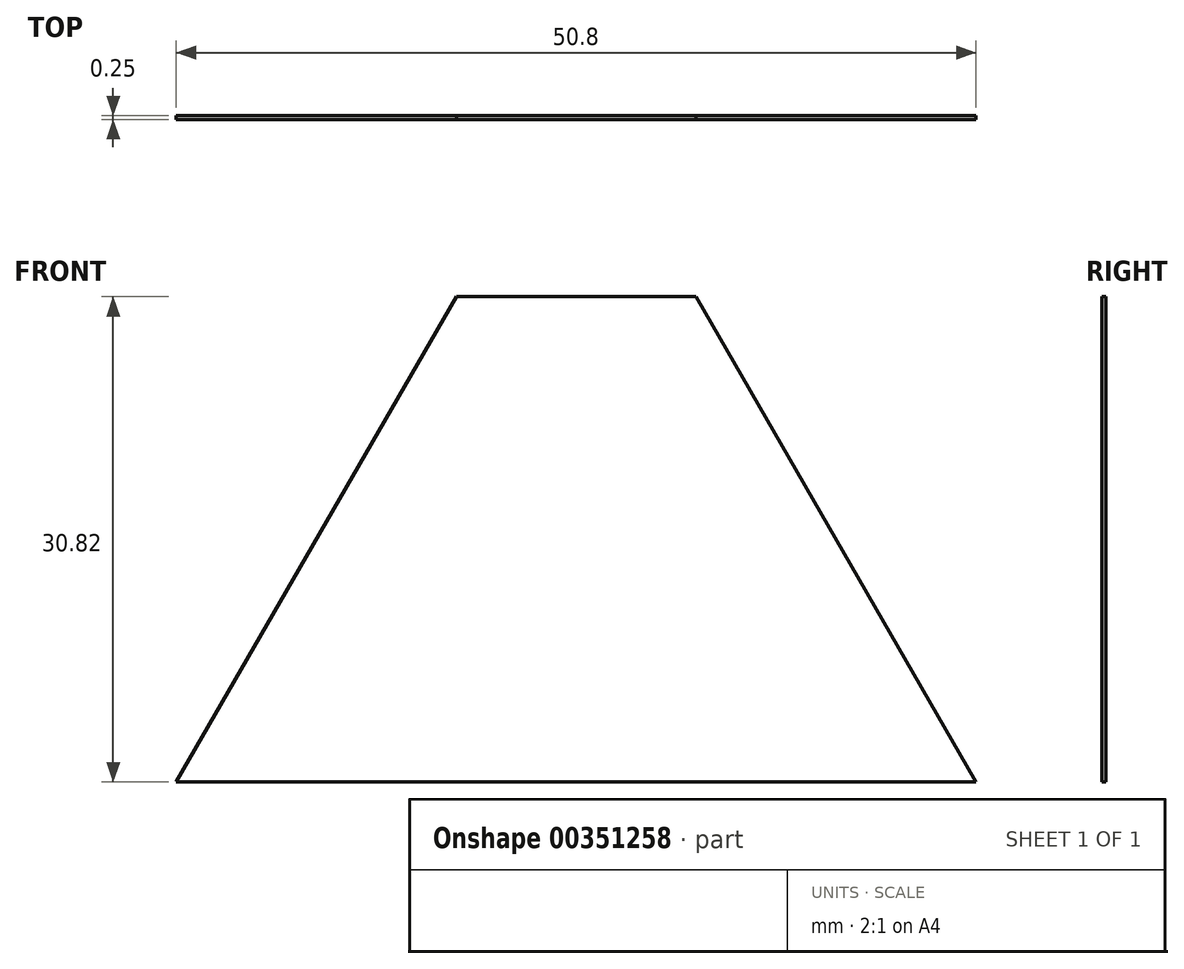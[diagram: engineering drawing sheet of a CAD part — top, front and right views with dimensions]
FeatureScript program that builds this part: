
annotation { "Feature Type Name" : "Feature", "Feature Type Description" : "" }
export const myFeature = defineFeature(function(context is Context, id is Id, definition is map)
    precondition{}
    {
        {
            var Q0;
            Q0=qCreatedBy(makeId("Front.planeOp"),FACE);
            var sketch = newSketch(context, id + "F0", { "sketchPlane" : qUnion([Q0])});
            skCircle(sketch, "E0.cCircle", {"center": v(0, 6.33) * mm, "radius": 14.66 * mm, "construction": true});
            skLineSegment(sketch, "E0.0", {"start": v(25.4, -8.33) * mm, "end": v(-25.4, -8.33) * mm});
            skLineSegment(sketch, "E0.1", {"start": v(-25.4, -8.33) * mm, "end": v(-7.6, 22.49) * mm});
            skLineSegment(sketch, "E0.2", {"start": v(7.6, 22.49) * mm, "end": v(25.4, -8.33) * mm});
            skPoint(sketch, "E0.0.midPoint", {"position": v(0, -8.33) * mm});
            skLineSegment(sketch, "E1", {"start": v(-7.6, 22.49) * mm, "end": v(7.6, 22.49) * mm});
            skPoint(sketch, "E2.orphan", {"position": v(0, 35.66) * mm});
            skSolve(sketch);
        }
        {
            var Q0;
            Q0=makeQuery(id+"F0.imprint","IMPRINT",FACE,{"disambiguationData":[TD([[makeQuery(id+"F0.imprint","IMPRINT",EDGE,{"derivedFrom":sQuery(id+"F0.wireOp",EDGE,"E0.0")}),-1.0]])]});
            extrude(context, id + "F1", {"entities" : qUnion([Q0]), "depth" : 0.25 * mm});
        }
    });
